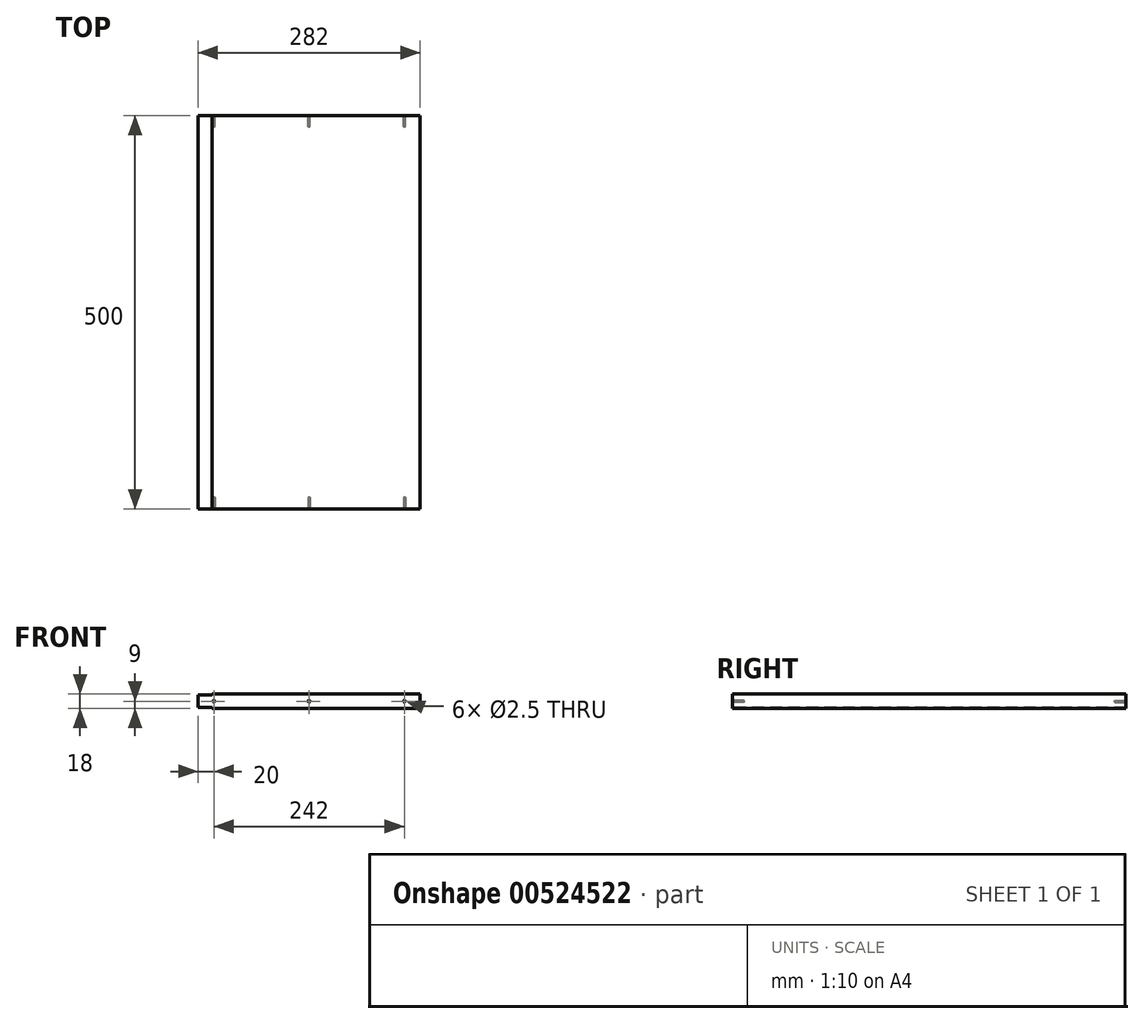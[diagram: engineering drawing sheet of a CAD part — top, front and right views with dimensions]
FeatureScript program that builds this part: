
annotation { "Feature Type Name" : "Feature", "Feature Type Description" : "" }
export const myFeature = defineFeature(function(context is Context, id is Id, definition is map)
    precondition{}
    {
        {
            var Q0;
            Q0=qCreatedBy(makeId("Top.planeOp"),FACE);
            var sketch = newSketch(context, id + "F0", { "sketchPlane" : qUnion([Q0])});
            skLineSegment(sketch, "E0.bottom", {"start": v(0, 0) * mm, "end": v(282, 0) * mm});
            skLineSegment(sketch, "E0.top", {"start": v(0, -500) * mm, "end": v(282, -500) * mm});
            skLineSegment(sketch, "E0.left", {"start": v(0, 0) * mm, "end": v(0, -500) * mm});
            skLineSegment(sketch, "E0.right", {"start": v(282, 0) * mm, "end": v(282, -500) * mm});
            skSolve(sketch);
        }
        {
            var Q0;
            Q0 = qSketchRegion(id + "F0", true);
            extrude(context, id + "F1", {"entities" : qUnion([Q0]), "depth" : 18 * mm, "offsetDistance" : 25 * mm});
        }
        {
            var Q0;
            Q0=makeQuery(id+"F1.opExtrude","SWEPT_FACE",FACE,{"disambiguationData":[OSD([sQuery(id+"F0.wireOp",EDGE,"E0.top")])]});
            var sketch = newSketch(context, id + "F2", { "sketchPlane" : qUnion([Q0])});
            skPoint(sketch, "E1", {"position": v(20, 9) * mm});
            skPoint(sketch, "E2", {"position": v(141, 9) * mm});
            skPoint(sketch, "E3", {"position": v(262, 9) * mm});
            skSolve(sketch);
        }
        {
            var Q0;
            Q0=sQuery(id+"F2.wireOp",VERTEX,"E1");
            var Q1;
            Q1=sQuery(id+"F2.wireOp",VERTEX,"E2");
            var Q2;
            Q2=sQuery(id+"F2.wireOp",VERTEX,"E3");
            var Q3;
            Q3=makeQuery(id+"F1.opExtrude","SWEPT_BODY",BODY,{"disambiguationData":[OSD([sQuery(id+"F0.wireOp",EDGE,"E0.bottom"),sQuery(id+"F0.wireOp",EDGE,"E0.top"),sQuery(id+"F0.wireOp",EDGE,"E0.left"),sQuery(id+"F0.wireOp",EDGE,"E0.right")])]});
            hole(context, id + "F3", {"style" : HoleStyle.SIMPLE, "endStyle" : HoleEndStyle.BLIND, "standardTappedOrClearance" : lookupTablePath({ "standard" : "ISO", "engagement" : "75%", "pitch" : "0.5 mm", "size" : "M3", "type" : "Tapped" }), "standardBlindInLast" : lookupTablePath({ "standard" : "ISO", "engagement" : "75%", "pitch" : "0.5 mm", "size" : "M3", "type" : "Tapped" }), "holeDiameter" : 2.5 * mm, "showTappedDepth" : true, "holeDepth" : 14.5 * mm, "isTappedThrough" : true, "tappedDepth" : 13 * mm, "tapClearance" : 3, "locations" : qUnion([Q0, Q1, Q2]), "scope" : qUnion([Q3]), "majorDiameter" : 3 * mm});
        }
        {
            var Q0;
            Q0=makeQuery(id+"F1.opExtrude","SWEPT_FACE",FACE,{"disambiguationData":[OSD([sQuery(id+"F0.wireOp",EDGE,"E0.bottom")])]});
            var sketch = newSketch(context, id + "F4", { "sketchPlane" : qUnion([Q0])});
            skPoint(sketch, "E4", {"position": v(-262, 9) * mm});
            skPoint(sketch, "E5", {"position": v(-141, 9) * mm});
            skPoint(sketch, "E6", {"position": v(-20, 9) * mm});
            skSolve(sketch);
        }
        {
            var Q0;
            Q0=sQuery(id+"F4.wireOp",VERTEX,"E4");
            var Q1;
            Q1=sQuery(id+"F4.wireOp",VERTEX,"E5");
            var Q2;
            Q2=sQuery(id+"F4.wireOp",VERTEX,"E6");
            var Q3;
            Q3=makeQuery(id+"F1.opExtrude","SWEPT_BODY",BODY,{"disambiguationData":[OSD([sQuery(id+"F0.wireOp",EDGE,"E0.bottom"),sQuery(id+"F0.wireOp",EDGE,"E0.top"),sQuery(id+"F0.wireOp",EDGE,"E0.left"),sQuery(id+"F0.wireOp",EDGE,"E0.right")])]});
            hole(context, id + "F5", {"style" : HoleStyle.SIMPLE, "endStyle" : HoleEndStyle.BLIND, "standardTappedOrClearance" : lookupTablePath({ "standard" : "ISO", "engagement" : "75%", "pitch" : "0.5 mm", "size" : "M3", "type" : "Tapped" }), "standardBlindInLast" : lookupTablePath({ "standard" : "ISO", "engagement" : "75%", "pitch" : "0.5 mm", "size" : "M3", "type" : "Tapped" }), "holeDiameter" : 2.5 * mm, "showTappedDepth" : true, "holeDepth" : 14 * mm, "isTappedThrough" : true, "tappedDepth" : 12.5 * mm, "tapClearance" : 3, "locations" : qUnion([Q0, Q1, Q2]), "scope" : qUnion([Q3]), "majorDiameter" : 3 * mm});
        }
        {
            var Q0;
            Q0=makeQuery(id+"F1.opExtrude","SWEPT_FACE",FACE,{"disambiguationData":[OSD([sQuery(id+"F0.wireOp",EDGE,"E0.top")])]});
            var sketch = newSketch(context, id + "F6", { "sketchPlane" : qUnion([Q0])});
            skLineSegment(sketch, "E7.bottom", {"start": v(0, 18) * mm, "end": v(18, 18) * mm});
            skLineSegment(sketch, "E7.top", {"start": v(0, 17) * mm, "end": v(18, 17) * mm});
            skLineSegment(sketch, "E7.left", {"start": v(0, 18) * mm, "end": v(0, 17) * mm});
            skLineSegment(sketch, "E7.right", {"start": v(18, 18) * mm, "end": v(18, 17) * mm});
            skLineSegment(sketch, "E8.bottom", {"start": v(0, 0) * mm, "end": v(18, 0) * mm});
            skLineSegment(sketch, "E8.top", {"start": v(0, 1) * mm, "end": v(18, 1) * mm});
            skLineSegment(sketch, "E8.left", {"start": v(0, 0) * mm, "end": v(0, 1) * mm});
            skLineSegment(sketch, "E8.right", {"start": v(18, 0) * mm, "end": v(18, 1) * mm});
            skSolve(sketch);
        }
        {
            var Q0;
            Q0 = qSketchRegion(id + "F6", true);
            extrude(context, id + "F7", {"entities" : qUnion([Q0]), "operationType" : NewBodyOperationType.REMOVE, "endBound" : BoundingType.THROUGH_ALL, "oppositeDirection" : true, "depth" : 25 * mm, "offsetDistance" : 25 * mm});
        }
    });
